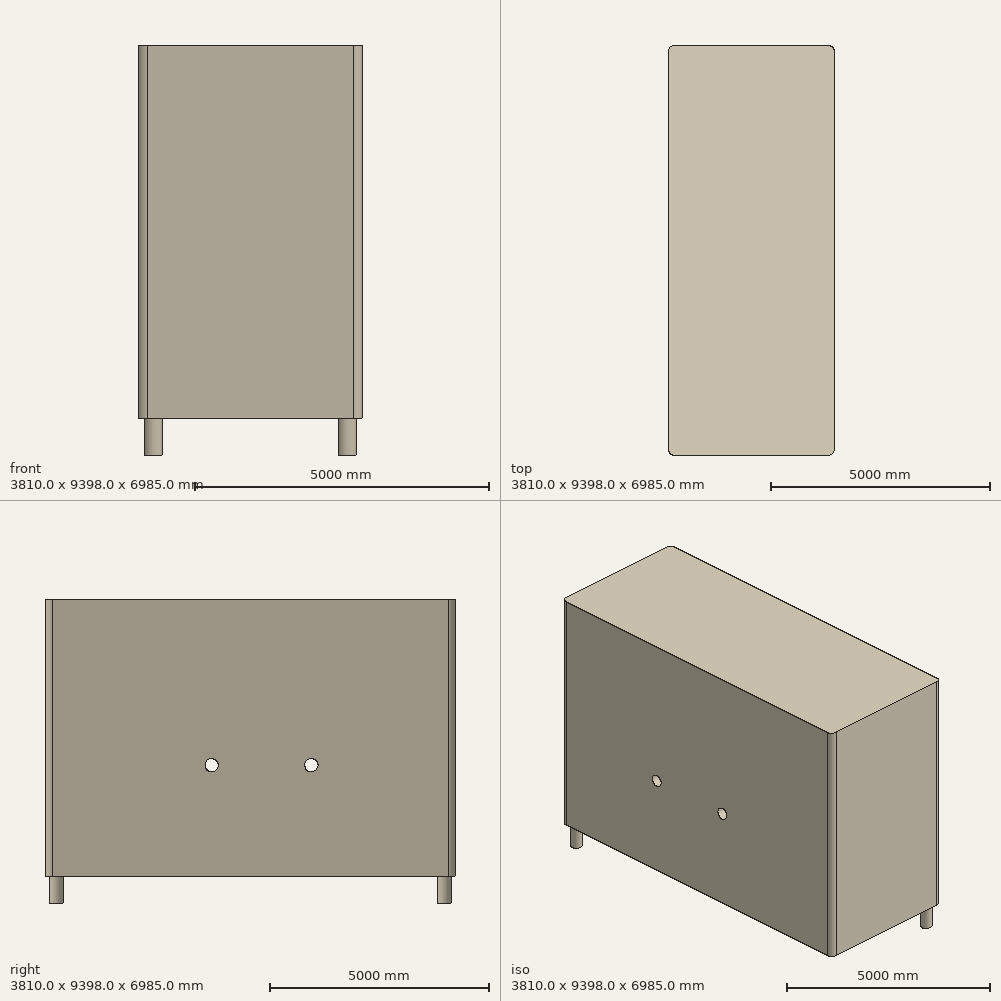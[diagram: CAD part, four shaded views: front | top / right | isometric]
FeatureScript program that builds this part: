
annotation { "Feature Type Name" : "Feature", "Feature Type Description" : "" }
export const myFeature = defineFeature(function(context is Context, id is Id, definition is map)
    precondition{}
    {
        {
            var Q0;
            Q0=qCreatedBy(makeId("Top.planeOp"),FACE);
            var sketch = newSketch(context, id + "F0", { "sketchPlane" : qUnion([Q0])});
            skLineSegment(sketch, "E0.bottom", {"start": v(-3517.8, -4118.06) * mm, "end": v(292.2, -4118.06) * mm});
            skLineSegment(sketch, "E0.top", {"start": v(-3517.8, 5279.94) * mm, "end": v(292.2, 5279.94) * mm});
            skLineSegment(sketch, "E0.left", {"start": v(-3517.8, -4118.06) * mm, "end": v(-3517.8, 5279.94) * mm});
            skLineSegment(sketch, "E0.right", {"start": v(292.2, -4118.06) * mm, "end": v(292.2, 5279.94) * mm});
            skLineSegment(sketch, "E1.bottom", {"start": v(-2882.8, 4644.94) * mm, "end": v(-342.8, 4644.94) * mm});
            skLineSegment(sketch, "E1.top", {"start": v(-2882.8, -3483.06) * mm, "end": v(-342.8, -3483.06) * mm});
            skLineSegment(sketch, "E1.left", {"start": v(-2882.8, 4644.94) * mm, "end": v(-2882.8, -3483.06) * mm});
            skLineSegment(sketch, "E1.right", {"start": v(-342.8, 4644.94) * mm, "end": v(-342.8, -3483.06) * mm});
            skLineSegment(sketch, "E2", {"start": v(-2882.8, 2739.94) * mm, "end": v(-342.8, 2739.94) * mm, "construction": true});
            skLineSegment(sketch, "E3", {"start": v(-2882.8, -1578.06) * mm, "end": v(-342.8, -1578.06) * mm, "construction": true});
            skLineSegment(sketch, "E4", {"start": v(-2882.8, 1723.94) * mm, "end": v(-3517.8, 1723.94) * mm, "construction": true});
            skLineSegment(sketch, "E5", {"start": v(-2882.8, 2079.54) * mm, "end": v(-3517.8, 2079.54) * mm});
            skLineSegment(sketch, "E6", {"start": v(-3517.8, 1368.34) * mm, "end": v(-2882.8, 1368.34) * mm});
            skLineSegment(sketch, "E7", {"start": v(-2882.8, -308.06) * mm, "end": v(-3517.8, -308.06) * mm, "construction": true});
            skLineSegment(sketch, "E8", {"start": v(-3517.8, -663.66) * mm, "end": v(-2882.8, -663.66) * mm});
            skLineSegment(sketch, "E9.MirrorCS", {"start": v(-3517.8, 47.54) * mm, "end": v(-2882.8, 47.54) * mm});
            skLineSegment(sketch, "E10", {"start": v(-1612.8, -4118.06) * mm, "end": v(-1612.8, 5279.94) * mm, "construction": true});
            skLineSegment(sketch, "E11.MirrorCS", {"start": v(-342.8, 2079.54) * mm, "end": v(292.2, 2079.54) * mm});
            skLineSegment(sketch, "E12.MirrorCS", {"start": v(292.2, 1368.34) * mm, "end": v(-342.8, 1368.34) * mm});
            skLineSegment(sketch, "E13.MirrorCS", {"start": v(-342.8, 1723.94) * mm, "end": v(292.2, 1723.94) * mm, "construction": true});
            skLineSegment(sketch, "E14.MirrorCS", {"start": v(292.2, 47.54) * mm, "end": v(-342.8, 47.54) * mm});
            skLineSegment(sketch, "E15.MirrorCS", {"start": v(292.2, -663.66) * mm, "end": v(-342.8, -663.66) * mm});
            skLineSegment(sketch, "E16.MirrorCS", {"start": v(-342.8, -308.06) * mm, "end": v(292.2, -308.06) * mm, "construction": true});
            skSolve(sketch);
        }
        {
            var Q0;
            {var subQ1=sQuery(id+"F0.wireOp",EDGE,"E0.top");Q0=makeQuery(id+"F0.imprint","IMPRINT",FACE,{"disambiguationData":[TD([[makeQuery(id+"F0.imprint","IMPRINT",EDGE,{"derivedFrom":subQ1}),-1.0]])]});}
            var Q1;
            {var subQ0=sQuery(id+"F0.wireOp",EDGE,"E11.MirrorCS");Q1=makeQuery(id+"F0.imprint","IMPRINT",FACE,{"disambiguationData":[TD([[makeQuery(id+"F0.imprint","IMPRINT",EDGE,{"derivedFrom":subQ0}),-1.0]])]});}
            var Q2;
            {var subQ4=sQuery(id+"F0.wireOp",EDGE,"E1.bottom");Q2=makeQuery(id+"F0.imprint","IMPRINT",FACE,{"disambiguationData":[TD([[makeQuery(id+"F0.imprint","IMPRINT",EDGE,{"derivedFrom":subQ4}),-1.0]])]});}
            var Q3;
            {var subQ0=sQuery(id+"F0.wireOp",EDGE,"E12.MirrorCS");Q3=makeQuery(id+"F0.imprint","IMPRINT",FACE,{"disambiguationData":[TD([[makeQuery(id+"F0.imprint","IMPRINT",EDGE,{"derivedFrom":subQ0}),1.0]])]});}
            var Q4;
            {var subQ2=sQuery(id+"F0.wireOp",EDGE,"E0.bottom");Q4=makeQuery(id+"F0.imprint","IMPRINT",FACE,{"disambiguationData":[TD([[makeQuery(id+"F0.imprint","IMPRINT",EDGE,{"derivedFrom":subQ2}),1.0]])]});}
            var Q5;
            {var subQ0=sQuery(id+"F0.wireOp",EDGE,"E14.MirrorCS");Q5=makeQuery(id+"F0.imprint","IMPRINT",FACE,{"disambiguationData":[TD([[makeQuery(id+"F0.imprint","IMPRINT",EDGE,{"derivedFrom":subQ0}),1.0]])]});}
            var Q6;
            {var subQ0=sQuery(id+"F0.wireOp",EDGE,"E8");Q6=makeQuery(id+"F0.imprint","IMPRINT",FACE,{"disambiguationData":[TD([[makeQuery(id+"F0.imprint","IMPRINT",EDGE,{"derivedFrom":subQ0}),1.0]])]});}
            var Q7;
            {var subQ0=sQuery(id+"F0.wireOp",EDGE,"E6");Q7=makeQuery(id+"F0.imprint","IMPRINT",FACE,{"disambiguationData":[TD([[makeQuery(id+"F0.imprint","IMPRINT",EDGE,{"derivedFrom":subQ0}),-1.0]])]});}
            var Q8;
            {var subQ0=sQuery(id+"F0.wireOp",EDGE,"E5");Q8=makeQuery(id+"F0.imprint","IMPRINT",FACE,{"disambiguationData":[TD([[makeQuery(id+"F0.imprint","IMPRINT",EDGE,{"derivedFrom":subQ0}),1.0]])]});}
            extrude(context, id + "F1", {"entities" : qUnion([Q0, Q1, Q2, Q3, Q4, Q5, Q6, Q7, Q8]), "depth" : 635 * mm, "offsetDistance" : 25.4 * mm});
        }
        {
            var Q0;
            {var subQ1=sQuery(id+"F0.wireOp",EDGE,"E0.top");Q0=makeQuery(id+"F0.imprint","IMPRINT",FACE,{"disambiguationData":[TD([[makeQuery(id+"F0.imprint","IMPRINT",EDGE,{"derivedFrom":subQ1}),-1.0]])]});}
            var Q1;
            {var subQ0=sQuery(id+"F0.wireOp",EDGE,"E5");Q1=makeQuery(id+"F0.imprint","IMPRINT",FACE,{"disambiguationData":[TD([[makeQuery(id+"F0.imprint","IMPRINT",EDGE,{"derivedFrom":subQ0}),1.0]])]});}
            var Q2;
            {var subQ0=sQuery(id+"F0.wireOp",EDGE,"E6");Q2=makeQuery(id+"F0.imprint","IMPRINT",FACE,{"disambiguationData":[TD([[makeQuery(id+"F0.imprint","IMPRINT",EDGE,{"derivedFrom":subQ0}),-1.0]])]});}
            var Q3;
            {var subQ0=sQuery(id+"F0.wireOp",EDGE,"E8");Q3=makeQuery(id+"F0.imprint","IMPRINT",FACE,{"disambiguationData":[TD([[makeQuery(id+"F0.imprint","IMPRINT",EDGE,{"derivedFrom":subQ0}),1.0]])]});}
            var Q4;
            {var subQ2=sQuery(id+"F0.wireOp",EDGE,"E0.bottom");Q4=makeQuery(id+"F0.imprint","IMPRINT",FACE,{"disambiguationData":[TD([[makeQuery(id+"F0.imprint","IMPRINT",EDGE,{"derivedFrom":subQ2}),1.0]])]});}
            var Q5;
            {var subQ0=sQuery(id+"F0.wireOp",EDGE,"E14.MirrorCS");Q5=makeQuery(id+"F0.imprint","IMPRINT",FACE,{"disambiguationData":[TD([[makeQuery(id+"F0.imprint","IMPRINT",EDGE,{"derivedFrom":subQ0}),1.0]])]});}
            var Q6;
            {var subQ0=sQuery(id+"F0.wireOp",EDGE,"E12.MirrorCS");Q6=makeQuery(id+"F0.imprint","IMPRINT",FACE,{"disambiguationData":[TD([[makeQuery(id+"F0.imprint","IMPRINT",EDGE,{"derivedFrom":subQ0}),1.0]])]});}
            var Q7;
            {var subQ0=sQuery(id+"F0.wireOp",EDGE,"E11.MirrorCS");Q7=makeQuery(id+"F0.imprint","IMPRINT",FACE,{"disambiguationData":[TD([[makeQuery(id+"F0.imprint","IMPRINT",EDGE,{"derivedFrom":subQ0}),-1.0]])]});}
            extrude(context, id + "F2", {"entities" : qUnion([Q0, Q1, Q2, Q3, Q4, Q5, Q6, Q7]), "operationType" : NewBodyOperationType.ADD, "oppositeDirection" : true, "depth" : 6350 * mm, "offsetDistance" : 25.4 * mm});
        }
        {
            var Q0;
            {var subQ0=sQuery(id+"F0.wireOp",EDGE,"E0.right");Q0=makeQuery(id+"F2.boolean.opBoolean","MERGE",FACE,{"derivedFrom":[makeQuery(id+"F1.opExtrude","SWEPT_FACE",FACE,{"disambiguationData":[OSD([subQ0])]}),makeQuery(id+"F2.opExtrude","SWEPT_FACE",FACE,{"disambiguationData":[OSD([subQ0])]})]});}
            var sketch = newSketch(context, id + "F3", { "sketchPlane" : qUnion([Q0])});
            skLineSegment(sketch, "E17.0", {"start": v(-4118.06, 0) * mm, "end": v(5279.94, 0) * mm});
            skPoint(sketch, "E18.0", {"position": v(1368.34, 0) * mm});
            skPoint(sketch, "E19.0", {"position": v(2079.54, 0) * mm});
            skLineSegment(sketch, "E20.0.0", {"start": v(-4118.06, 635) * mm, "end": v(-4118.06, -6350) * mm});
            skLineSegment(sketch, "E20.0.1", {"start": v(-4118.06, -6350) * mm, "end": v(5279.94, -6350) * mm});
            skLineSegment(sketch, "E20.0.2", {"start": v(5279.94, -6350) * mm, "end": v(5279.94, 635) * mm});
            skLineSegment(sketch, "E20.0.3", {"start": v(5279.94, 635) * mm, "end": v(-4118.06, 635) * mm});
            skPoint(sketch, "E21.0", {"position": v(47.54, 0) * mm});
            skPoint(sketch, "E22.0", {"position": v(-663.66, 0) * mm});
            skPoint(sketch, "E23.0", {"position": v(-308.06, 0) * mm});
            skPoint(sketch, "E24.0", {"position": v(1723.94, 0) * mm});
            skLineSegment(sketch, "E25", {"start": v(735.04, 0) * mm, "end": v(735.04, -6350) * mm, "construction": true});
            skLineSegment(sketch, "E26", {"start": v(1977.94, -20.38) * mm, "end": v(1977.94, -5093.92) * mm, "construction": true});
            skLineSegment(sketch, "E27", {"start": v(-308.06, 0) * mm, "end": v(-308.06, -5093.92) * mm, "construction": true});
            skLineSegment(sketch, "E28", {"start": v(1977.94, -3175) * mm, "end": v(-308.06, -3175) * mm, "construction": true});
            skPoint(sketch, "E28.startSnap0", {"position": v(735.04, -3175) * mm});
            skCircle(sketch, "E29", {"center": v(1977.94, -3175) * mm, "radius": 355.6 * mm});
            skCircle(sketch, "E30", {"center": v(-308.06, -3175) * mm, "radius": 355.6 * mm});
            skSolve(sketch);
        }
        {
            var Q0;
            Q0=makeQuery(id+"F3.imprint","IMPRINT",FACE,{"disambiguationData":[TD([[makeQuery(id+"F3.imprint","IMPRINT",EDGE,{"derivedFrom":sQuery(id+"F3.wireOp",EDGE,"E29")}),1.0]])]});
            var Q1;
            Q1=makeQuery(id+"F3.imprint","IMPRINT",FACE,{"disambiguationData":[TD([[makeQuery(id+"F3.imprint","IMPRINT",EDGE,{"derivedFrom":sQuery(id+"F3.wireOp",EDGE,"E30")}),1.0]])]});
            extrude(context, id + "F4", {"entities" : qUnion([Q0, Q1]), "operationType" : NewBodyOperationType.REMOVE, "endBound" : BoundingType.THROUGH_ALL, "oppositeDirection" : true, "depth" : 25.4 * mm, "offsetDistance" : 25.4 * mm});
        }
        {
            var Q0;
            {var subQ0=sQuery(id+"F0.wireOp",EDGE,"E0.left");var subQ1=sQuery(id+"F0.wireOp",EDGE,"E0.top");Q0=makeQuery(id+"F2.boolean.opBoolean","MERGE",EDGE,{"derivedFrom":[makeQuery(id+"F1.opExtrude","SWEPT_EDGE",EDGE,{"disambiguationData":[OSD([subQ1,subQ0])]}),makeQuery(id+"F2.opExtrude","SWEPT_EDGE",EDGE,{"disambiguationData":[OSD([subQ1,subQ0])]})]});}
            var Q1;
            {var subQ0=sQuery(id+"F0.wireOp",EDGE,"E0.right");var subQ1=sQuery(id+"F0.wireOp",EDGE,"E0.top");Q1=makeQuery(id+"F2.boolean.opBoolean","MERGE",EDGE,{"derivedFrom":[makeQuery(id+"F1.opExtrude","SWEPT_EDGE",EDGE,{"disambiguationData":[OSD([subQ1,subQ0])]}),makeQuery(id+"F2.opExtrude","SWEPT_EDGE",EDGE,{"disambiguationData":[OSD([subQ1,subQ0])]})]});}
            var Q2;
            {var subQ0=sQuery(id+"F0.wireOp",EDGE,"E0.left");var subQ1=sQuery(id+"F0.wireOp",EDGE,"E0.bottom");Q2=makeQuery(id+"F2.boolean.opBoolean","MERGE",EDGE,{"derivedFrom":[makeQuery(id+"F1.opExtrude","SWEPT_EDGE",EDGE,{"disambiguationData":[OSD([subQ1,subQ0])]}),makeQuery(id+"F2.opExtrude","SWEPT_EDGE",EDGE,{"disambiguationData":[OSD([subQ1,subQ0])]})]});}
            var Q3;
            {var subQ0=sQuery(id+"F0.wireOp",EDGE,"E0.right");var subQ1=sQuery(id+"F0.wireOp",EDGE,"E0.bottom");Q3=makeQuery(id+"F2.boolean.opBoolean","MERGE",EDGE,{"derivedFrom":[makeQuery(id+"F1.opExtrude","SWEPT_EDGE",EDGE,{"disambiguationData":[OSD([subQ1,subQ0])]}),makeQuery(id+"F2.opExtrude","SWEPT_EDGE",EDGE,{"disambiguationData":[OSD([subQ1,subQ0])]})]});}
            fillet(context, id + "F5", {"entities" : qUnion([Q0, Q1, Q2, Q3]), "radius" : 152.4 * mm, "tangentPropagation" : true, "allowEdgeOverflow" : false});
        }
        {
            var Q0;
            {var subQ0=sQuery(id+"F0.wireOp",EDGE,"E0.right");Q0=makeQuery(id+"F2.boolean.opBoolean","MERGE",FACE,{"derivedFrom":[makeQuery(id+"F1.opExtrude","SWEPT_FACE",FACE,{"disambiguationData":[OSD([subQ0])]}),makeQuery(id+"F2.opExtrude","SWEPT_FACE",FACE,{"disambiguationData":[OSD([subQ0])]})]});}
            var sketch = newSketch(context, id + "F6", { "sketchPlane" : qUnion([Q0])});
            skCircle(sketch, "E31.0", {"center": v(1977.94, -3175) * mm, "radius": 355.6 * mm});
            skCircle(sketch, "E32.0", {"center": v(-308.06, -3175) * mm, "radius": 355.6 * mm});
            skCircle(sketch, "E33", {"center": v(1977.94, -3175) * mm, "radius": 152.4 * mm});
            skCircle(sketch, "E34", {"center": v(-308.06, -3175) * mm, "radius": 152.4 * mm});
            skSolve(sketch);
        }
        {
            var Q0;
            Q0=makeQuery(id+"F6.imprint","IMPRINT",FACE,{"disambiguationData":[TD([[makeQuery(id+"F6.imprint","IMPRINT",EDGE,{"derivedFrom":sQuery(id+"F6.wireOp",EDGE,"E31.0")}),1.0]])]});
            var Q1;
            Q1=makeQuery(id+"F6.imprint","IMPRINT",FACE,{"disambiguationData":[TD([[makeQuery(id+"F6.imprint","IMPRINT",EDGE,{"derivedFrom":sQuery(id+"F6.wireOp",EDGE,"E32.0")}),1.0]])]});
            extrude(context, id + "F7", {"entities" : qUnion([Q0, Q1]), "operationType" : NewBodyOperationType.ADD, "oppositeDirection" : true, "depth" : 431.8 * mm, "offsetDistance" : 25.4 * mm});
        }
        {
            var Q0;
            {var subQ0=sQuery(id+"F0.wireOp",EDGE,"E0.left");Q0=makeQuery(id+"F2.boolean.opBoolean","MERGE",FACE,{"derivedFrom":[makeQuery(id+"F1.opExtrude","SWEPT_FACE",FACE,{"disambiguationData":[OSD([subQ0])]}),makeQuery(id+"F2.opExtrude","SWEPT_FACE",FACE,{"disambiguationData":[OSD([subQ0])]})]});}
            var sketch = newSketch(context, id + "F8", { "sketchPlane" : qUnion([Q0])});
            skCircle(sketch, "E35.0", {"center": v(308.06, -3175) * mm, "radius": 355.6 * mm});
            skCircle(sketch, "E36.0", {"center": v(-1977.94, -3175) * mm, "radius": 355.6 * mm});
            skCircle(sketch, "E37", {"center": v(308.06, -3175) * mm, "radius": 152.4 * mm});
            skCircle(sketch, "E38", {"center": v(-1977.94, -3175) * mm, "radius": 152.4 * mm});
            skSolve(sketch);
        }
        {
            var Q0;
            Q0=makeQuery(id+"F8.imprint","IMPRINT",FACE,{"disambiguationData":[TD([[makeQuery(id+"F8.imprint","IMPRINT",EDGE,{"derivedFrom":sQuery(id+"F8.wireOp",EDGE,"E35.0")}),1.0]])]});
            var Q1;
            Q1=makeQuery(id+"F8.imprint","IMPRINT",FACE,{"disambiguationData":[TD([[makeQuery(id+"F8.imprint","IMPRINT",EDGE,{"derivedFrom":sQuery(id+"F8.wireOp",EDGE,"E36.0")}),1.0]])]});
            extrude(context, id + "F9", {"entities" : qUnion([Q0, Q1]), "operationType" : NewBodyOperationType.ADD, "oppositeDirection" : true, "depth" : 431.8 * mm, "offsetDistance" : 25.4 * mm});
        }
        {
            var Q0;
            Q0=makeQuery(id+"F2.opExtrude","CAP_FACE",FACE,{"disambiguationData":[OSD([sQuery(id+"F0.wireOp",EDGE,"E0.bottom"),sQuery(id+"F0.wireOp",EDGE,"E0.top"),sQuery(id+"F0.wireOp",EDGE,"E0.left"),sQuery(id+"F0.wireOp",EDGE,"E0.right"),sQuery(id+"F0.wireOp",EDGE,"E1.bottom"),sQuery(id+"F0.wireOp",EDGE,"E1.top"),sQuery(id+"F0.wireOp",EDGE,"E1.left"),sQuery(id+"F0.wireOp",EDGE,"E1.right")])],"isStart":false});
            var sketch = newSketch(context, id + "F10", { "sketchPlane" : qUnion([Q0])});
            skLineSegment(sketch, "E39", {"start": v(-1612.8, 4118.06) * mm, "end": v(-1612.8, -5279.94) * mm, "construction": true});
            skLineSegment(sketch, "E40", {"start": v(-3517.8, -580.94) * mm, "end": v(417.39, -580.94) * mm, "construction": true});
            skCircle(sketch, "E41", {"center": v(-3263.8, 3864.06) * mm, "radius": 152.4 * mm});
            skCircle(sketch, "E42.MirrorC", {"center": v(38.2, 3864.06) * mm, "radius": 152.4 * mm});
            skLineSegment(sketch, "E43.MirrorCS", {"start": v(292.2, -580.94) * mm, "end": v(-3643, -580.94) * mm, "construction": true});
            skCircle(sketch, "E44.MirrorC", {"center": v(38.2, -5025.94) * mm, "radius": 152.4 * mm});
            skCircle(sketch, "E45.MirrorC", {"center": v(-3263.8, -5025.94) * mm, "radius": 152.4 * mm});
            skSolve(sketch);
        }
        {
            var Q0;
            Q0=makeQuery(id+"F10.imprint","IMPRINT",FACE,{"disambiguationData":[TD([[makeQuery(id+"F10.imprint","IMPRINT",EDGE,{"derivedFrom":sQuery(id+"F10.wireOp",EDGE,"E41")}),1.0]])]});
            var Q1;
            Q1=makeQuery(id+"F10.imprint","IMPRINT",FACE,{"disambiguationData":[TD([[makeQuery(id+"F10.imprint","IMPRINT",EDGE,{"derivedFrom":sQuery(id+"F10.wireOp",EDGE,"E42.MirrorC")}),-1.0]])]});
            var Q2;
            Q2=makeQuery(id+"F10.imprint","IMPRINT",FACE,{"disambiguationData":[TD([[makeQuery(id+"F10.imprint","IMPRINT",EDGE,{"derivedFrom":sQuery(id+"F10.wireOp",EDGE,"E44.MirrorC")}),1.0]])]});
            var Q3;
            Q3=makeQuery(id+"F10.imprint","IMPRINT",FACE,{"disambiguationData":[TD([[makeQuery(id+"F10.imprint","IMPRINT",EDGE,{"derivedFrom":sQuery(id+"F10.wireOp",EDGE,"E45.MirrorC")}),-1.0]])]});
            extrude(context, id + "F11", {"entities" : qUnion([Q0, Q1, Q2, Q3]), "operationType" : NewBodyOperationType.REMOVE, "oppositeDirection" : true, "depth" : 635 * mm, "offsetDistance" : 25.4 * mm});
        }
    });
